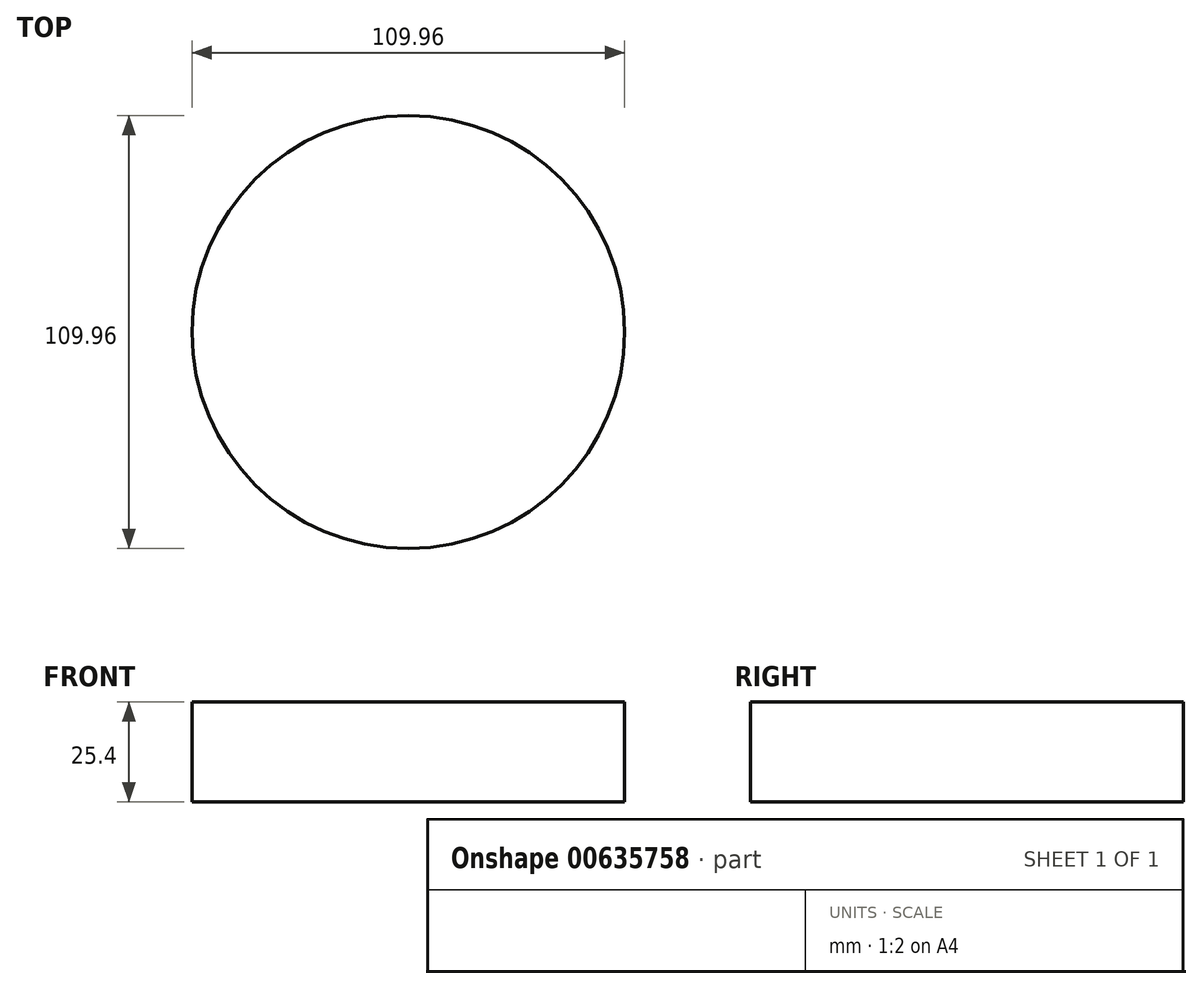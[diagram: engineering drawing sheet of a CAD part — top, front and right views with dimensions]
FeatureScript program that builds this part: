
annotation { "Feature Type Name" : "Feature", "Feature Type Description" : "" }
export const myFeature = defineFeature(function(context is Context, id is Id, definition is map)
    precondition{}
    {
        {
            var Q0;
            Q0=qCreatedBy(makeId("Top.planeOp"),FACE);
            var sketch = newSketch(context, id + "F0", { "sketchPlane" : qUnion([Q0])});
            skCircle(sketch, "E0", {"center": v(0, 0) * mm, "radius": 54.98 * mm});
            skSolve(sketch);
        }
        {
            var Q0;
            Q0=makeQuery(id+"F0.imprint","IMPRINT",FACE,{"disambiguationData":[TD([[makeQuery(id+"F0.imprint","IMPRINT",EDGE,{"derivedFrom":sQuery(id+"F0.wireOp",EDGE,"E0")}),1.0]])]});
            extrude(context, id + "F1", {"entities" : qUnion([Q0]), "depth" : 25.4 * mm, "offsetDistance" : 25.4 * mm});
        }
    });
